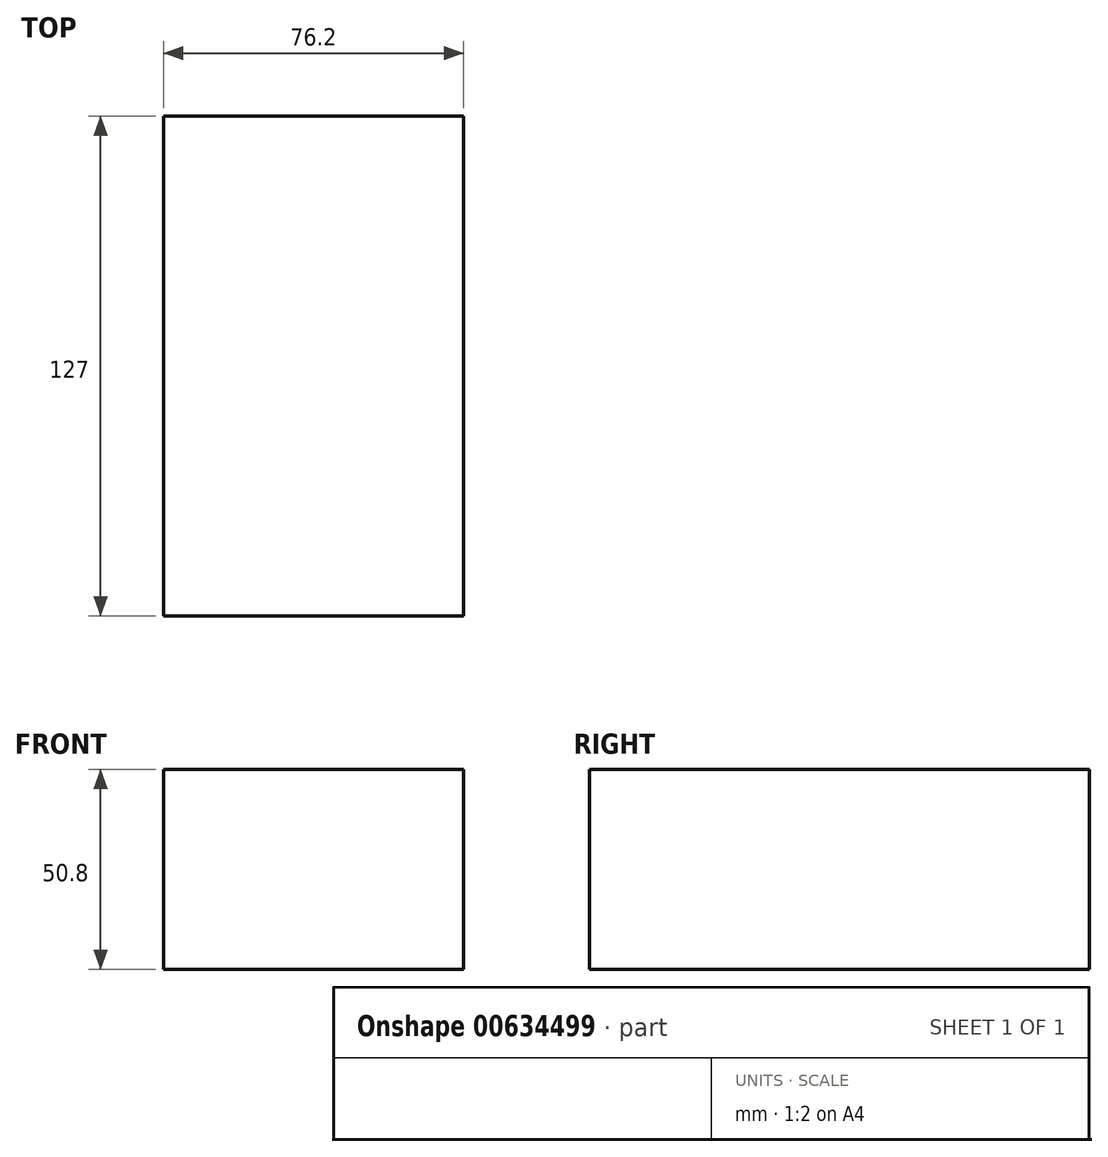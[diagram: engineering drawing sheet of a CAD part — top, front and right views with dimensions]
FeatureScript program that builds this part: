
annotation { "Feature Type Name" : "Feature", "Feature Type Description" : "" }
export const myFeature = defineFeature(function(context is Context, id is Id, definition is map)
    precondition{}
    {
        {
            var Q0;
            Q0=qCreatedBy(makeId("Front.planeOp"),FACE);
            var sketch = newSketch(context, id + "F0", { "sketchPlane" : qUnion([Q0])});
            skLineSegment(sketch, "E0.bottom", {"start": v(0, 0) * mm, "end": v(76.2, 0) * mm});
            skLineSegment(sketch, "E0.top", {"start": v(0, 50.8) * mm, "end": v(76.2, 50.8) * mm});
            skLineSegment(sketch, "E0.left", {"start": v(0, 0) * mm, "end": v(0, 50.8) * mm});
            skLineSegment(sketch, "E0.right", {"start": v(76.2, 0) * mm, "end": v(76.2, 50.8) * mm});
            skSolve(sketch);
        }
        {
            var Q0;
            Q0=qSketchRegion(id+"F0",true);
            extrude(context, id + "F1", {"entities" : qUnion([Q0]), "oppositeDirection" : true, "depth" : 127 * mm});
        }
    });
